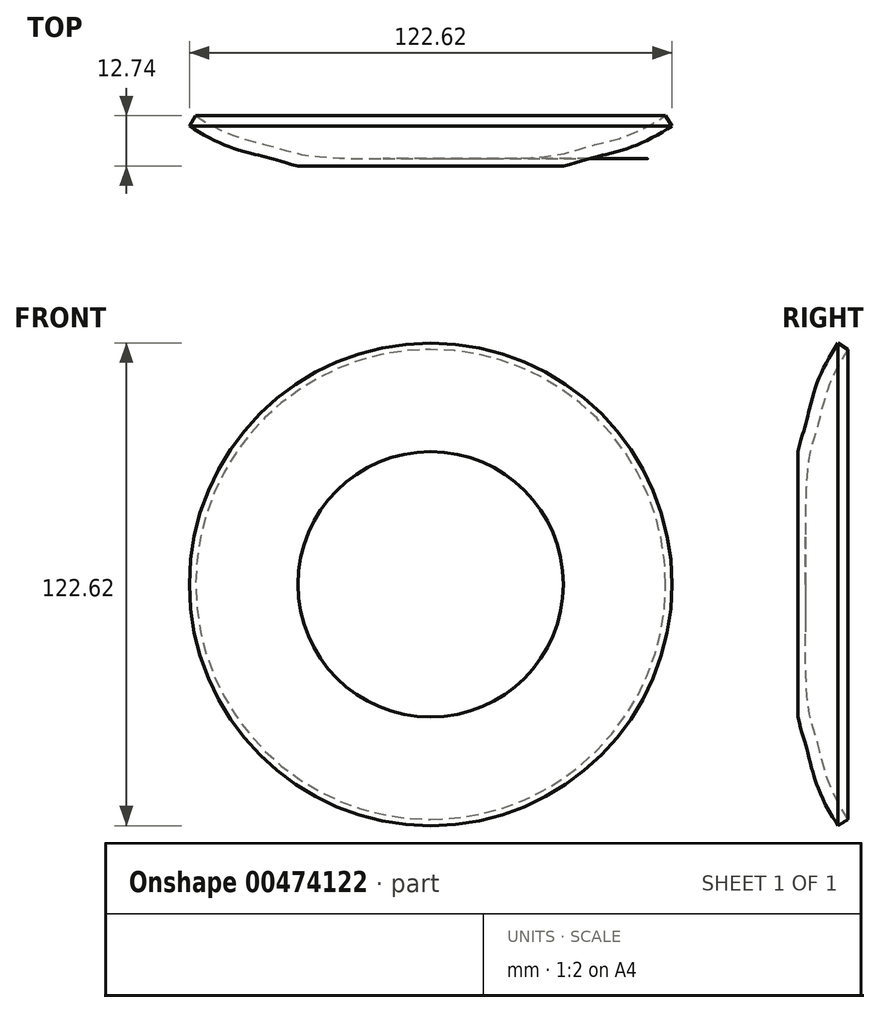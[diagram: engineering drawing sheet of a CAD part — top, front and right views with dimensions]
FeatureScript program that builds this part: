
annotation { "Feature Type Name" : "Feature", "Feature Type Description" : "" }
export const myFeature = defineFeature(function(context is Context, id is Id, definition is map)
    precondition{}
    {
        {
            var Q0;
            Q0=qCreatedBy(makeId("Top.planeOp"),FACE);
            var sketch = newSketch(context, id + "F0", { "sketchPlane" : qUnion([Q0])});
            skLineSegment(sketch, "E0", {"start": v(0, 0) * mm, "end": v(0, 3.18) * mm});
            skFitSpline(sketch, "E1", {"points": [v(0, 3.18) * mm, v(30.85, 3.89) * mm, v(39.35, 6.01) * mm, v(47.57, 8.16) * mm, v(53.95, 10.71) * mm, v(59.7, 14) * mm], "startDerivative": vector(101.72, -0.41) * mm, "endDerivative": vector(37.23, 23.22) * mm});
            skFitSpline(sketch, "E2.0", {"points": [v(-0.01, 0.13) * mm, v(2.1, 0.12) * mm, v(6.42, 0.09) * mm, v(12.91, 0.06) * mm, v(19.15, 0.1) * mm, v(23.94, 0.25) * mm, v(27.4, 0.46) * mm, v(29.79, 0.67) * mm, v(31.96, 0.95) * mm, v(33.86, 1.3) * mm, v(35.54, 1.7) * mm, v(37.04, 2.12) * mm, v(38.4, 2.54) * mm, v(39.48, 2.87) * mm, v(40.33, 3.12) * mm, v(41, 3.3) * mm, v(41.68, 3.48) * mm, v(42.64, 3.72) * mm, v(43.87, 4.03) * mm, v(45.4, 4.4) * mm, v(46.67, 4.73) * mm, v(47.69, 5.01) * mm, v(48.45, 5.24) * mm, v(49.2, 5.47) * mm, v(50.16, 5.79) * mm, v(51.34, 6.21) * mm, v(52.7, 6.76) * mm, v(54.43, 7.53) * mm, v(56.52, 8.58) * mm, v(58.94, 9.96) * mm, v(60.52, 10.93) * mm, v(61.3, 11.42) * mm]});
            skLineSegment(sketch, "E3", {"start": v(59.7, 14) * mm, "end": v(61.3, 11.42) * mm});
            skLineSegment(sketch, "E4", {"start": v(0.05, 0.13) * mm, "end": v(0, 0) * mm});
            skSolve(sketch);
        }
        {
            var Q0;
            Q0 = qSketchRegion(id + "F0", true);
            var Q1;
            Q1=sQuery(id+"F0.wireOp",EDGE,"E0");
            revolve(context, id + "F1", {"entities" : qUnion([Q0]), "axis" : qUnion([Q1]), "revolveType" : RevolveType.FULL});
        }
        {
            var Q0;
            Q0=qCreatedBy(makeId("Front.planeOp"),FACE);
            var sketch = newSketch(context, id + "F2", { "sketchPlane" : qUnion([Q0])});
            skLineSegment(sketch, "E5", {"start": v(-51.95, -66.15) * mm, "end": v(56.4, -66.15) * mm});
            skLineSegment(sketch, "E6", {"start": v(56.4, -66.15) * mm, "end": v(56.4, 63) * mm});
            skLineSegment(sketch, "E7", {"start": v(56.4, 63) * mm, "end": v(-63.87, 63) * mm});
            skLineSegment(sketch, "E8", {"start": v(-63.87, 63) * mm, "end": v(-63.87, -66.66) * mm});
            skLineSegment(sketch, "E9", {"start": v(-63.87, -66.66) * mm, "end": v(-51.95, -66.15) * mm});
            skSolve(sketch);
        }
        {
            var Q0;
            Q0 = qSketchRegion(id + "F2", true);
            extrude(context, id + "F3", {"entities" : qUnion([Q0]), "operationType" : NewBodyOperationType.REMOVE, "endBound" : BoundingType.SYMMETRIC, "oppositeDirection" : true, "depth" : 2.54 * mm});
        }
    });
